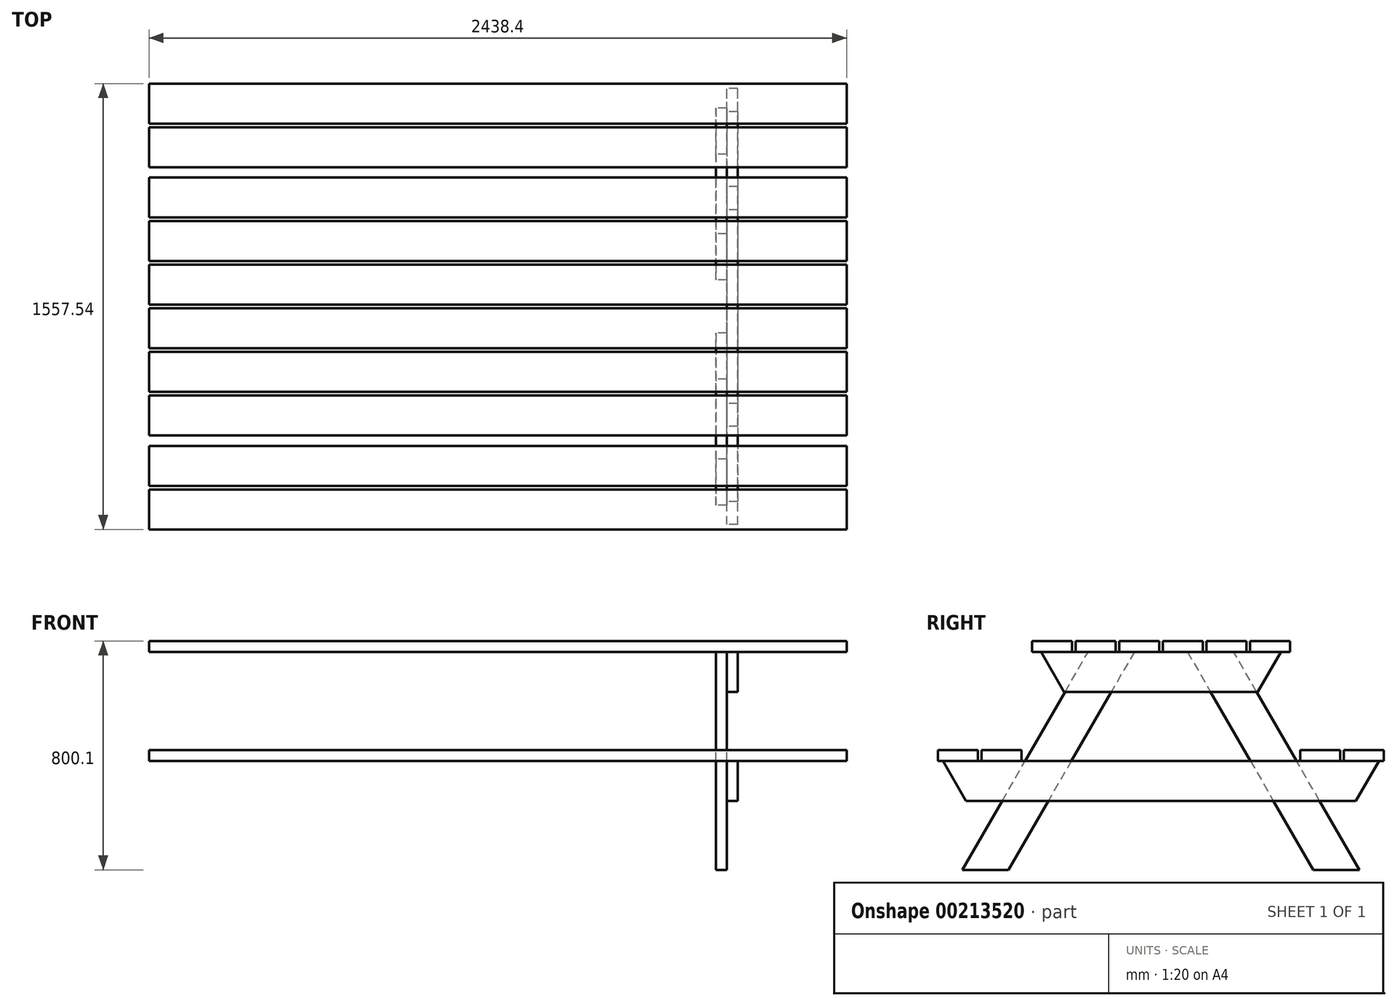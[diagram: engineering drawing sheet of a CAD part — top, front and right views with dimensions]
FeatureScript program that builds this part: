
annotation { "Feature Type Name" : "Feature", "Feature Type Description" : "" }
export const myFeature = defineFeature(function(context is Context, id is Id, definition is map)
    precondition{}
    {
        {
            var Q0;
            Q0=qCreatedBy(makeId("Right.planeOp"),FACE);
            var sketch = newSketch(context, id + "F0", { "sketchPlane" : qUnion([Q0])});
            skLineSegment(sketch, "E0", {"start": v(-693.94, 0) * mm, "end": v(-254, 762) * mm});
            skLineSegment(sketch, "E1", {"start": v(-254, 762) * mm, "end": v(-92.69, 762) * mm});
            skLineSegment(sketch, "E2", {"start": v(-92.69, 762) * mm, "end": v(-532.63, 0) * mm});
            skLineSegment(sketch, "E3", {"start": v(-532.63, 0) * mm, "end": v(-693.94, 0) * mm});
            skLineSegment(sketch, "E4.MirrorCS", {"start": v(92.69, 762) * mm, "end": v(532.63, 0) * mm});
            skLineSegment(sketch, "E5.MirrorCS", {"start": v(693.94, 0) * mm, "end": v(254, 762) * mm});
            skLineSegment(sketch, "E6.MirrorCS", {"start": v(254, 762) * mm, "end": v(92.69, 762) * mm});
            skLineSegment(sketch, "E7.MirrorCS", {"start": v(532.63, 0) * mm, "end": v(693.94, 0) * mm});
            skSolve(sketch);
        }
        {
            var Q0;
            Q0 = qSketchRegion(id + "F0", true);
            extrude(context, id + "F1", {"entities" : qUnion([Q0]), "depth" : 38.1 * mm});
        }
        {
            var Q0;
            Q0=makeQuery(id+"F1.opExtrude","CAP_FACE",FACE,{"disambiguationData":[OSD([sQuery(id+"F0.wireOp",EDGE,"E0"),sQuery(id+"F0.wireOp",EDGE,"E1"),sQuery(id+"F0.wireOp",EDGE,"E2"),sQuery(id+"F0.wireOp",EDGE,"E3")])],"isStart":false});
            var sketch = newSketch(context, id + "F2", { "sketchPlane" : qUnion([Q0])});
            skLineSegment(sketch, "E8", {"start": v(-762, 381) * mm, "end": v(762, 381) * mm});
            skLineSegment(sketch, "E9", {"start": v(681.34, 241.3) * mm, "end": v(762, 381) * mm});
            skLineSegment(sketch, "E10", {"start": v(681.34, 241.3) * mm, "end": v(-681.34, 241.3) * mm});
            skLineSegment(sketch, "E11", {"start": v(-762, 381) * mm, "end": v(-681.34, 241.3) * mm});
            skLineSegment(sketch, "E12", {"start": v(0, 0) * mm, "end": v(0, 1132.93) * mm, "construction": true});
            skLineSegment(sketch, "E13", {"start": v(-419.1, 762) * mm, "end": v(419.1, 762) * mm});
            skPoint(sketch, "E13.endSnap0", {"position": v(-173.34, 762) * mm});
            skLineSegment(sketch, "E14", {"start": v(419.1, 762) * mm, "end": v(338.44, 622.3) * mm});
            skLineSegment(sketch, "E15", {"start": v(338.44, 622.3) * mm, "end": v(-338.44, 622.3) * mm});
            skLineSegment(sketch, "E16", {"start": v(-338.44, 622.3) * mm, "end": v(-419.1, 762) * mm});
            skSolve(sketch);
        }
        {
            var Q0;
            Q0 = qSketchRegion(id + "F2", true);
            extrude(context, id + "F3", {"entities" : qUnion([Q0]), "operationType" : NewBodyOperationType.ADD, "depth" : 38.1 * mm});
        }
        {
            var Q0;
            Q0=makeQuery(id+"F3.opExtrude","CAP_FACE",FACE,{"disambiguationData":[OSD([sQuery(id+"F2.wireOp",EDGE,"E13"),sQuery(id+"F2.wireOp",EDGE,"E14"),sQuery(id+"F2.wireOp",EDGE,"E15"),sQuery(id+"F2.wireOp",EDGE,"E16")])],"isStart":false});
            var sketch = newSketch(context, id + "F4", { "sketchPlane" : qUnion([Q0])});
            skLineSegment(sketch, "E17.bottom", {"start": v(-778.77, 419.1) * mm, "end": v(-639.07, 419.1) * mm});
            skLineSegment(sketch, "E17.top", {"start": v(-778.77, 381) * mm, "end": v(-639.07, 381) * mm});
            skLineSegment(sketch, "E17.left", {"start": v(-778.77, 419.1) * mm, "end": v(-778.77, 381) * mm});
            skLineSegment(sketch, "E17.right", {"start": v(-639.07, 419.1) * mm, "end": v(-639.07, 381) * mm});
            skLineSegment(sketch, "E18.bottom", {"start": v(-626.37, 419.1) * mm, "end": v(-486.67, 419.1) * mm});
            skLineSegment(sketch, "E18.top", {"start": v(-626.37, 381) * mm, "end": v(-486.67, 381) * mm});
            skLineSegment(sketch, "E18.left", {"start": v(-626.37, 419.1) * mm, "end": v(-626.37, 381) * mm});
            skLineSegment(sketch, "E18.right", {"start": v(-486.67, 419.1) * mm, "end": v(-486.67, 381) * mm});
            skLineSegment(sketch, "E19", {"start": v(0, 0) * mm, "end": v(0, 544.01) * mm, "construction": true});
            skLineSegment(sketch, "E20.MirrorCS", {"start": v(486.67, 419.1) * mm, "end": v(486.67, 381) * mm});
            skLineSegment(sketch, "E21.MirrorCS", {"start": v(626.37, 419.1) * mm, "end": v(626.37, 381) * mm});
            skLineSegment(sketch, "E22.MirrorCS", {"start": v(626.37, 381) * mm, "end": v(486.67, 381) * mm});
            skLineSegment(sketch, "E23.MirrorCS", {"start": v(626.37, 419.1) * mm, "end": v(486.67, 419.1) * mm});
            skLineSegment(sketch, "E24.MirrorCS", {"start": v(639.07, 419.1) * mm, "end": v(639.07, 381) * mm});
            skLineSegment(sketch, "E25.MirrorCS", {"start": v(778.77, 419.1) * mm, "end": v(778.77, 381) * mm});
            skLineSegment(sketch, "E26.MirrorCS", {"start": v(778.77, 381) * mm, "end": v(639.07, 381) * mm});
            skLineSegment(sketch, "E27.MirrorCS", {"start": v(778.77, 419.1) * mm, "end": v(639.07, 419.1) * mm});
            skLineSegment(sketch, "E28.bottom", {"start": v(-310.6, 762) * mm, "end": v(-450.3, 762) * mm});
            skLineSegment(sketch, "E28.top", {"start": v(-310.6, 800.1) * mm, "end": v(-450.3, 800.1) * mm});
            skLineSegment(sketch, "E28.left", {"start": v(-310.6, 762) * mm, "end": v(-310.6, 800.1) * mm});
            skLineSegment(sketch, "E28.right", {"start": v(-450.3, 762) * mm, "end": v(-450.3, 800.1) * mm});
            skLineSegment(sketch, "E29.1.0.0", {"start": v(-297.9, 762) * mm, "end": v(-297.9, 800.1) * mm});
            skLineSegment(sketch, "E29.1.0.1", {"start": v(-158.2, 800.1) * mm, "end": v(-297.9, 800.1) * mm});
            skLineSegment(sketch, "E29.1.0.2", {"start": v(-158.2, 762) * mm, "end": v(-158.2, 800.1) * mm});
            skLineSegment(sketch, "E29.1.0.3", {"start": v(-158.2, 762) * mm, "end": v(-297.9, 762) * mm});
            skLineSegment(sketch, "E29.2.0.0", {"start": v(-145.5, 762) * mm, "end": v(-145.5, 800.1) * mm});
            skLineSegment(sketch, "E29.2.0.1", {"start": v(-5.8, 800.1) * mm, "end": v(-145.5, 800.1) * mm});
            skLineSegment(sketch, "E29.2.0.2", {"start": v(-5.8, 762) * mm, "end": v(-5.8, 800.1) * mm});
            skLineSegment(sketch, "E29.2.0.3", {"start": v(-5.8, 762) * mm, "end": v(-145.5, 762) * mm});
            skLineSegment(sketch, "E29.3.0.0", {"start": v(6.9, 762) * mm, "end": v(6.9, 800.1) * mm});
            skLineSegment(sketch, "E29.3.0.1", {"start": v(146.6, 800.1) * mm, "end": v(6.9, 800.1) * mm});
            skLineSegment(sketch, "E29.3.0.2", {"start": v(146.6, 762) * mm, "end": v(146.6, 800.1) * mm});
            skLineSegment(sketch, "E29.3.0.3", {"start": v(146.6, 762) * mm, "end": v(6.9, 762) * mm});
            skLineSegment(sketch, "E29.4.0.0", {"start": v(159.3, 762) * mm, "end": v(159.3, 800.1) * mm});
            skLineSegment(sketch, "E29.4.0.1", {"start": v(299, 800.1) * mm, "end": v(159.3, 800.1) * mm});
            skLineSegment(sketch, "E29.4.0.2", {"start": v(299, 762) * mm, "end": v(299, 800.1) * mm});
            skLineSegment(sketch, "E29.4.0.3", {"start": v(299, 762) * mm, "end": v(159.3, 762) * mm});
            skLineSegment(sketch, "E29.5.0.0", {"start": v(311.7, 762) * mm, "end": v(311.7, 800.1) * mm});
            skLineSegment(sketch, "E29.5.0.1", {"start": v(451.4, 800.1) * mm, "end": v(311.7, 800.1) * mm});
            skLineSegment(sketch, "E29.5.0.2", {"start": v(451.4, 762) * mm, "end": v(451.4, 800.1) * mm});
            skLineSegment(sketch, "E29.5.0.3", {"start": v(451.4, 762) * mm, "end": v(311.7, 762) * mm});
            skLineSegment(sketch, "E29.direction1", {"start": v(-450.3, 762) * mm, "end": v(-297.9, 762) * mm, "construction": true});
            skSolve(sketch);
        }
        {
            var Q0;
            Q0 = qSketchRegion(id + "F4", true);
            extrude(context, id + "F5", {"entities" : qUnion([Q0]), "operationType" : NewBodyOperationType.ADD, "depth" : 381 * mm, "hasSecondDirection" : true, "secondDirectionOppositeDirection" : true, "secondDirectionDepth" : 2057.4 * mm});
        }
        {
            var Q0;
            Q0=makeQuery(id+"F5.opExtrude","SWEPT_EDGE",EDGE,{"disambiguationData":[OSD([sQuery(id+"F4.wireOp",EDGE,"E28.top"),sQuery(id+"F4.wireOp",EDGE,"E28.right")])]});
            cPoint(context, id + "F6", {"entities" : qUnion([Q0]), "parameter" : 0.5});
        }
        {
            var Q0;
            Q0=makeQuery(id+"F3.opExtrude","CAP_FACE",FACE,{"disambiguationData":[OSD([sQuery(id+"F2.wireOp",EDGE,"E8"),sQuery(id+"F2.wireOp",EDGE,"E9"),sQuery(id+"F2.wireOp",EDGE,"E10"),sQuery(id+"F2.wireOp",EDGE,"E11")])],"isStart":false});
            var Q1;
            Q1 = qCreatedBy(id + "F6" ,VERTEX);
            cPlane(context, id + "F7", {"entities" : qUnion([Q0, Q1]), "cplaneType" : CPlaneType.PLANE_POINT, "offset" : 25.4 * mm, "width" : 152.4 * mm, "height" : 152.4 * mm});
        }
    });
